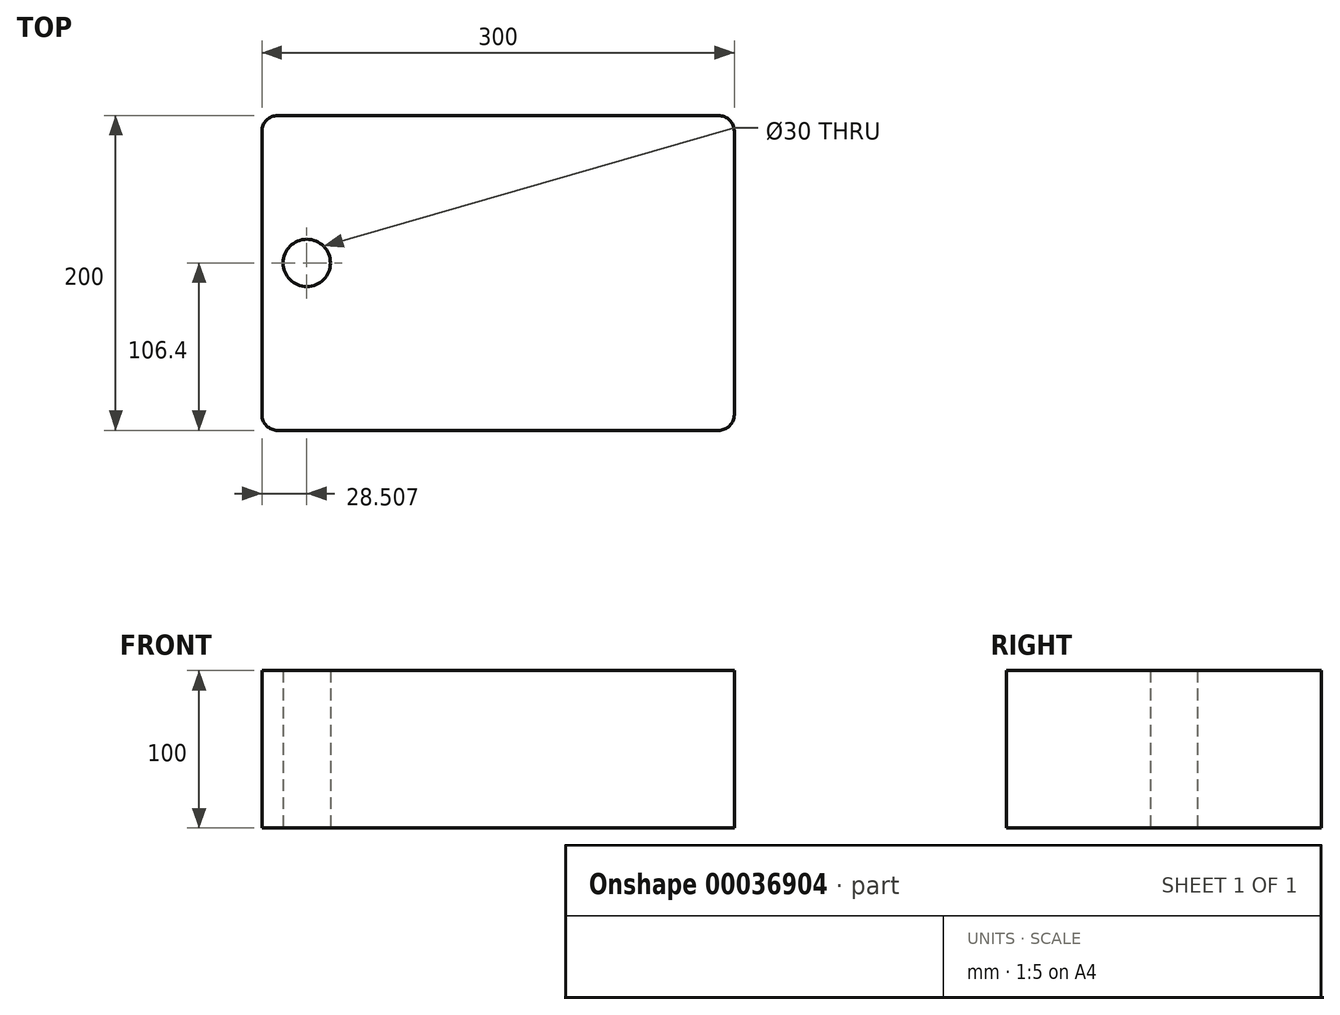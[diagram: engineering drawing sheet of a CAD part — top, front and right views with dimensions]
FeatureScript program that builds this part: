
annotation { "Feature Type Name" : "Feature", "Feature Type Description" : "" }
export const myFeature = defineFeature(function(context is Context, id is Id, definition is map)
    precondition{}
    {
        {
            var Q0;
            Q0=qCreatedBy(makeId("Top.planeOp"),FACE);
            var sketch = newSketch(context, id + "F0", { "sketchPlane" : qUnion([Q0])});
            skLineSegment(sketch, "E0.bottom", {"start": v(-150.84, 93.6) * mm, "end": v(149.16, 93.6) * mm});
            skLineSegment(sketch, "E0.top", {"start": v(-150.84, -106.4) * mm, "end": v(149.16, -106.4) * mm});
            skLineSegment(sketch, "E0.left", {"start": v(-150.84, 93.6) * mm, "end": v(-150.84, -106.4) * mm});
            skLineSegment(sketch, "E0.right", {"start": v(149.16, 93.6) * mm, "end": v(149.16, -106.4) * mm});
            skCircle(sketch, "E1", {"center": v(-122.33, 0) * mm, "radius": 15 * mm});
            skSolve(sketch);
        }
        {
            var Q0;
            Q0=makeQuery(id+"F0.imprint","IMPRINT",FACE,{"disambiguationData":[TD([[makeQuery(id+"F0.imprint","IMPRINT",EDGE,{"derivedFrom":sQuery(id+"F0.wireOp",EDGE,"E0.bottom")}),-1.0]])]});
            extrude(context, id + "F1", {"entities" : qUnion([Q0]), "depth" : 100 * mm});
        }
        {
            var Q0;
            Q0=makeQuery(id+"F1.opExtrude","SWEPT_EDGE",EDGE,{"disambiguationData":[OSD([sQuery(id+"F0.wireOp",EDGE,"E0.bottom"),sQuery(id+"F0.wireOp",EDGE,"E0.right")])]});
            var Q1;
            Q1=makeQuery(id+"F1.opExtrude","SWEPT_EDGE",EDGE,{"disambiguationData":[OSD([sQuery(id+"F0.wireOp",EDGE,"E0.top"),sQuery(id+"F0.wireOp",EDGE,"E0.right")])]});
            var Q2;
            Q2=makeQuery(id+"F1.opExtrude","SWEPT_EDGE",EDGE,{"disambiguationData":[OSD([sQuery(id+"F0.wireOp",EDGE,"E0.bottom"),sQuery(id+"F0.wireOp",EDGE,"E0.left")])]});
            var Q3;
            Q3=makeQuery(id+"F1.opExtrude","SWEPT_EDGE",EDGE,{"disambiguationData":[OSD([sQuery(id+"F0.wireOp",EDGE,"E0.top"),sQuery(id+"F0.wireOp",EDGE,"E0.left")])]});
            fillet(context, id + "F2", {"entities" : qUnion([Q0, Q1, Q2, Q3]), "radius" : 10 * mm, "tangentPropagation" : true, "allowEdgeOverflow" : false});
        }
    });
